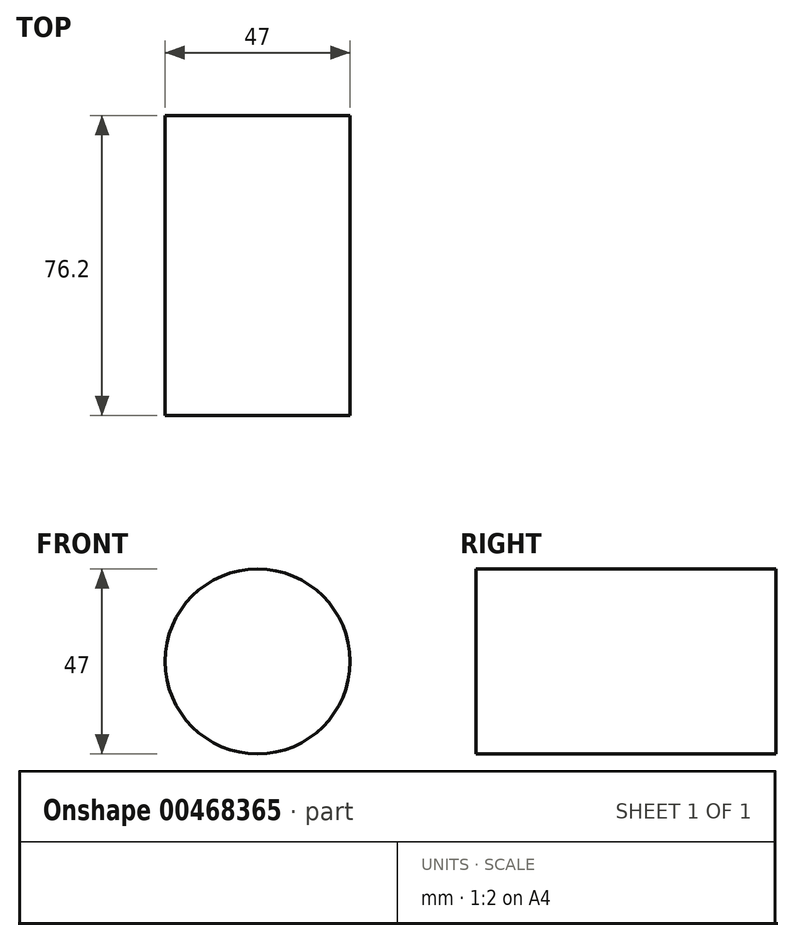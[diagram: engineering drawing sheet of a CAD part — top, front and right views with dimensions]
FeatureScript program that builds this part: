
annotation { "Feature Type Name" : "Feature", "Feature Type Description" : "" }
export const myFeature = defineFeature(function(context is Context, id is Id, definition is map)
    precondition{}
    {
        {
            var Q0;
            Q0=qCreatedBy(makeId("Front.planeOp"),FACE);
            var sketch = newSketch(context, id + "F0", { "sketchPlane" : qUnion([Q0])});
            skCircle(sketch, "E0", {"center": v(0, 0) * mm, "radius": 23.5 * mm});
            skSolve(sketch);
        }
        {
            var Q0;
            Q0 = qSketchRegion(id + "F0", true);
            extrude(context, id + "F1", {"entities" : qUnion([Q0]), "depth" : 76.2 * mm});
        }
    });
